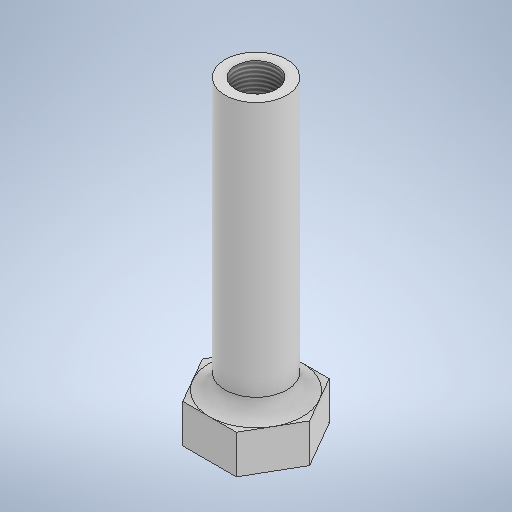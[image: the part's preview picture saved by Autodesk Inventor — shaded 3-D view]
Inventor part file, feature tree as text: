
AUTODESK INVENTOR PART (.ipt)
format: ipt  version: 2025.2 (Build 292293000, 293)  size: 269,824 bytes
history: native  units: mm
features: extrude x3, sketch x3, other x1, thread x1, fillet x1
ambient origin geometry x8: Origin, YZ Plane, XZ Plane, XY Plane, X Axis, Y Axis, Z Axis, Center Point
bodies: Body1 (feature_tree)
feature tree (9):
  other  "Bryła1"
  extrude  "Wyciągnięcie proste1"  Depth=8.0mm
  extrude  "Wyciągnięcie proste2"  Depth=35.0mm TaperAngle=0.0deg
  thread  "Gwint1"
  extrude  "Wyciągnięcie proste3"  Depth=5.3mm
  fillet  "Zaokrąglenie1"  Radius=25.0mm
  sketch  "Szkic1"
  sketch  "Szkic2"
  sketch  "Szkic3"
